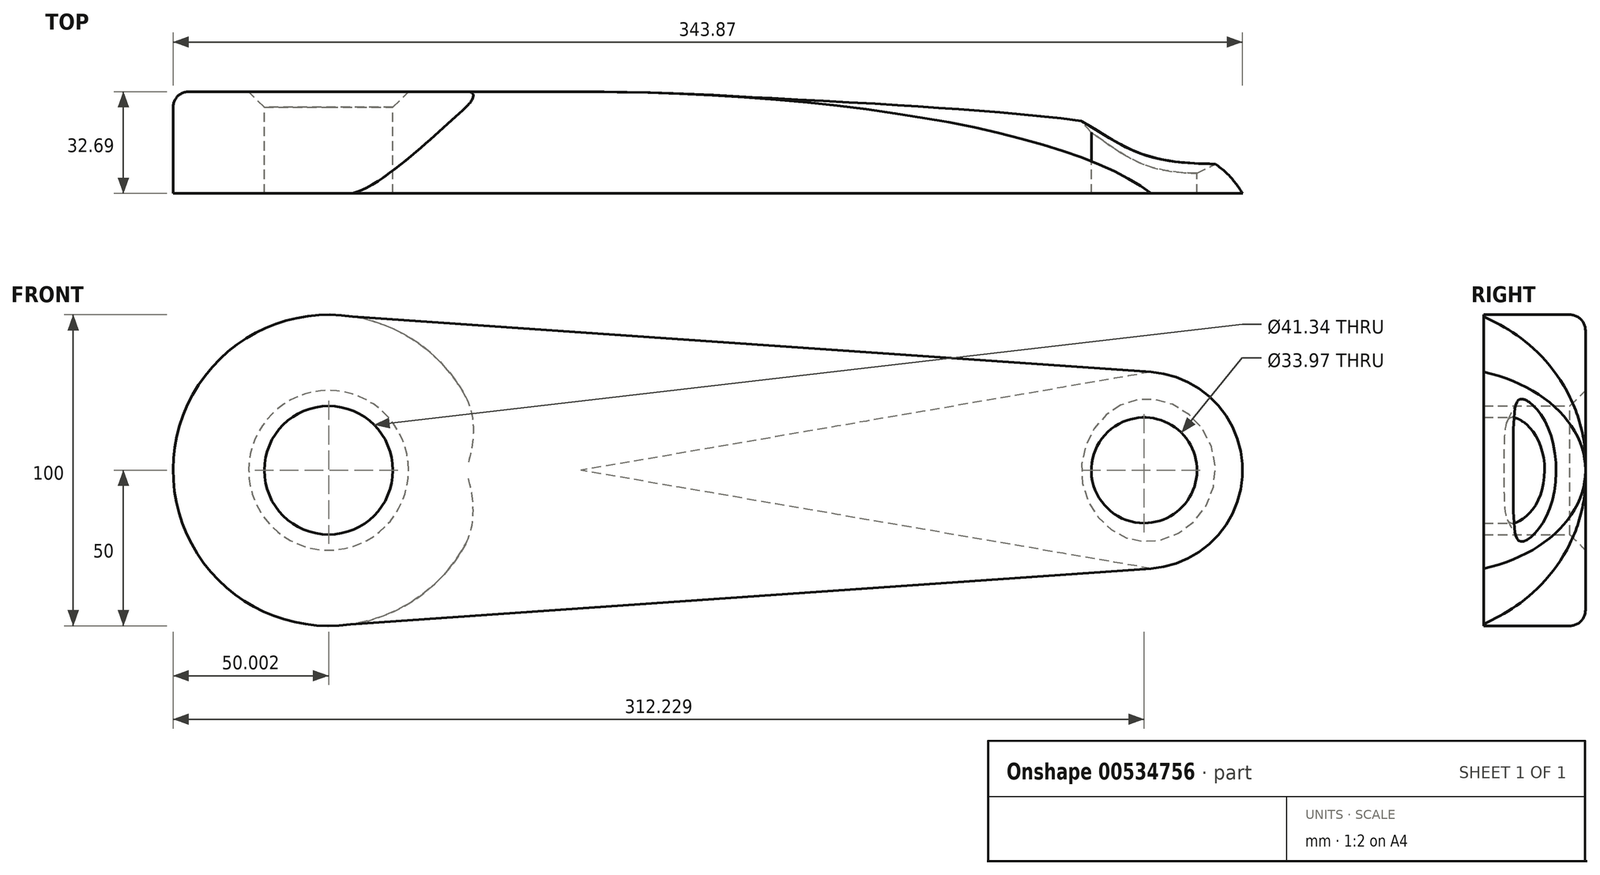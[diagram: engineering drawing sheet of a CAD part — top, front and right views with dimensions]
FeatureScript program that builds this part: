
annotation { "Feature Type Name" : "Feature", "Feature Type Description" : "" }
export const myFeature = defineFeature(function(context is Context, id is Id, definition is map)
    precondition{}
    {
        {
            var Q0;
            Q0=qCreatedBy(makeId("Front.planeOp"),FACE);
            var sketch = newSketch(context, id + "F0", { "sketchPlane" : qUnion([Q0])});
            skCircle(sketch, "E0", {"center": v(-127.76, 0) * mm, "radius": 50 * mm});
            skCircle(sketch, "E1", {"center": v(134.47, 0) * mm, "radius": 31.64 * mm});
            skLineSegment(sketch, "E2", {"start": v(-128.55, 50) * mm, "end": v(136.66, 31.57) * mm});
            skLineSegment(sketch, "E3", {"start": v(-127.83, -50) * mm, "end": v(136.67, -31.57) * mm});
            skCircle(sketch, "E4", {"center": v(-127.76, 0) * mm, "radius": 20.67 * mm});
            skCircle(sketch, "E5", {"center": v(134.47, 0) * mm, "radius": 16.99 * mm});
            skSolve(sketch);
        }
        {
            var Q0;
            Q0=makeQuery(id+"F0.imprint","IMPRINT",FACE,{"disambiguationData":[TD([[makeQuery(id+"F0.imprint","IMPRINT",EDGE,{"derivedFrom":sQuery(id+"F0.wireOp",EDGE,"E4")}),-1.0]])]});
            var Q1;
            Q1 = qSketchRegion(id + "F0", true);
            var Q2;
            {var subQ0=sQuery(id+"F0.wireOp",EDGE,"E2");var subQ1=sQuery(id+"F0.wireOp",EDGE,"E0");var subQ2=makeQuery(id+"F0.imprint","INTERSECT",VERTEX,{"disambiguationData":[OD(1.0)],"derivedFrom":[subQ1,subQ0]});Q2=makeQuery(id+"F0.imprint","IMPRINT",FACE,{"disambiguationData":[TD([[makeQuery(id+"F0.imprint","IMPRINT",EDGE,{"disambiguationData":[TD([[subQ2,1.0]])],"derivedFrom":subQ1}),-1.0]])]});}
            var Q3;
            Q3=makeQuery(id+"F0.imprint","IMPRINT",FACE,{"disambiguationData":[TD([[makeQuery(id+"F0.imprint","IMPRINT",EDGE,{"derivedFrom":sQuery(id+"F0.wireOp",EDGE,"E5")}),-1.0]])]});
            extrude(context, id + "F1", {"entities" : qUnion([Q0, Q1, Q2, Q3]), "depth" : 32.7 * mm, "offsetDistance" : 25 * mm});
        }
        {
            var Q0;
            Q0=makeQuery(id+"F1.opExtrude","CAP_EDGE",EDGE,{"disambiguationData":[OSD([sQuery(id+"F0.wireOp",EDGE,"E4")])],"isStart":true});
            chamfer(context, id + "F2", {"entities" : qUnion([Q0]), "width" : 5 * mm, "tangentPropagation" : true});
        }
        {
            var Q0;
            Q0=makeQuery(id+"F1.opExtrude","CAP_EDGE",EDGE,{"disambiguationData":[OSD([sQuery(id+"F0.wireOp",EDGE,"E3")])],"isStart":true});
            fillet(context, id + "F3", {"entities" : qUnion([Q0]), "radius" : 46.25 * mm, "tangentPropagation" : true, "allowEdgeOverflow" : false});
        }
        {
            var Q0;
            Q0=makeQuery(id+"F1.opExtrude","CAP_EDGE",EDGE,{"disambiguationData":[OSD([sQuery(id+"F0.wireOp",EDGE,"E0")])],"isStart":true});
            fillet(context, id + "F4", {"entities" : qUnion([Q0]), "radius" : 5 * mm, "tangentPropagation" : true, "allowEdgeOverflow" : false});
        }
        {
            var Q0;
            Q0=makeQuery(id+"F3.opFillet","BLEND_EDGE",EDGE,{"blendedFrom":[makeQuery(id+"F1.opExtrude","CAP_EDGE",EDGE,{"disambiguationData":[OSD([sQuery(id+"F0.wireOp",EDGE,"E3")])],"isStart":true}),makeQuery(id+"F1.opExtrude","SWEPT_FACE",FACE,{"disambiguationData":[OSD([sQuery(id+"F0.wireOp",EDGE,"E5")])]})],"blendedInto":[makeQuery(id+"F1.opExtrude","SWEPT_FACE",FACE,{"disambiguationData":[OSD([sQuery(id+"F0.wireOp",EDGE,"E5")])]})]});
            chamfer(context, id + "F5", {"entities" : qUnion([Q0]), "chamferType" : ChamferType.TWO_OFFSETS, "width1" : 5 * mm, "oppositeDirection" : false, "width2" : 5 * mm, "tangentPropagation" : true});
        }
    });
